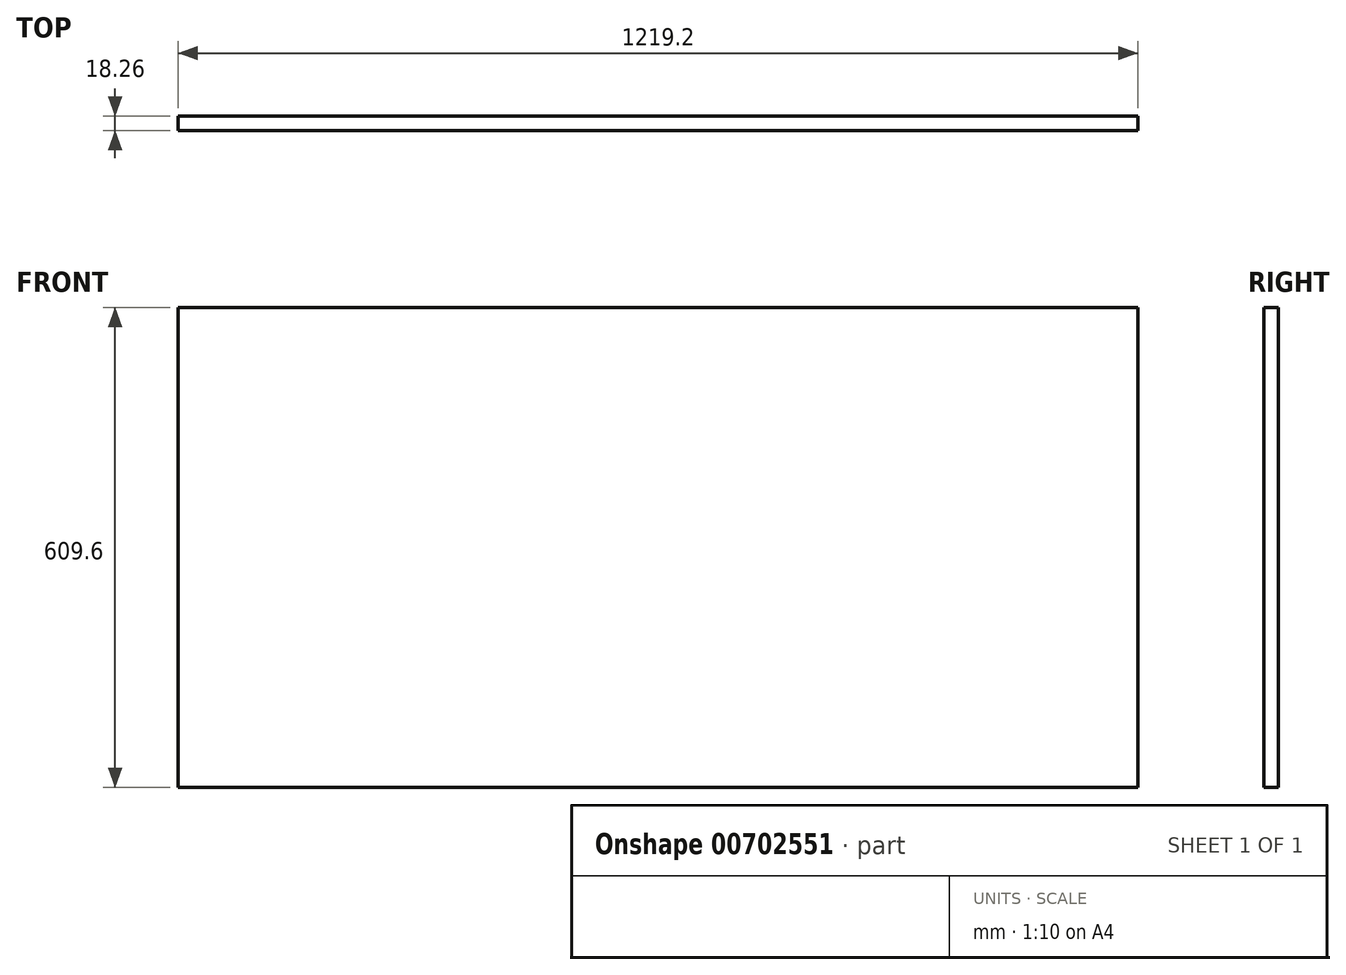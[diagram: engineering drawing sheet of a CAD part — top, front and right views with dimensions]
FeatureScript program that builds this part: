
annotation { "Feature Type Name" : "Feature", "Feature Type Description" : "" }
export const myFeature = defineFeature(function(context is Context, id is Id, definition is map)
    precondition{}
    {
        {
            var Q0;
            Q0=qCreatedBy(makeId("Front.planeOp"),FACE);
            var sketch = newSketch(context, id + "F0", { "sketchPlane" : qUnion([Q0])});
            skLineSegment(sketch, "E0.bottom", {"start": v(0, 0) * mm, "end": v(1219.2, 0) * mm});
            skLineSegment(sketch, "E0.top", {"start": v(0, 609.6) * mm, "end": v(1219.2, 609.6) * mm});
            skLineSegment(sketch, "E0.left", {"start": v(0, 0) * mm, "end": v(0, 609.6) * mm});
            skLineSegment(sketch, "E0.right", {"start": v(1219.2, 0) * mm, "end": v(1219.2, 609.6) * mm});
            skSolve(sketch);
        }
        {
            var Q0;
            Q0=makeQuery(id+"F0.imprint","IMPRINT",FACE,{"disambiguationData":[TD([[makeQuery(id+"F0.imprint","IMPRINT",EDGE,{"derivedFrom":sQuery(id+"F0.wireOp",EDGE,"E0.bottom")}),1.0]])]});
            extrude(context, id + "F1", {"entities" : qUnion([Q0]), "depth" : 18.26 * mm, "offsetDistance" : 25.4 * mm});
        }
    });
